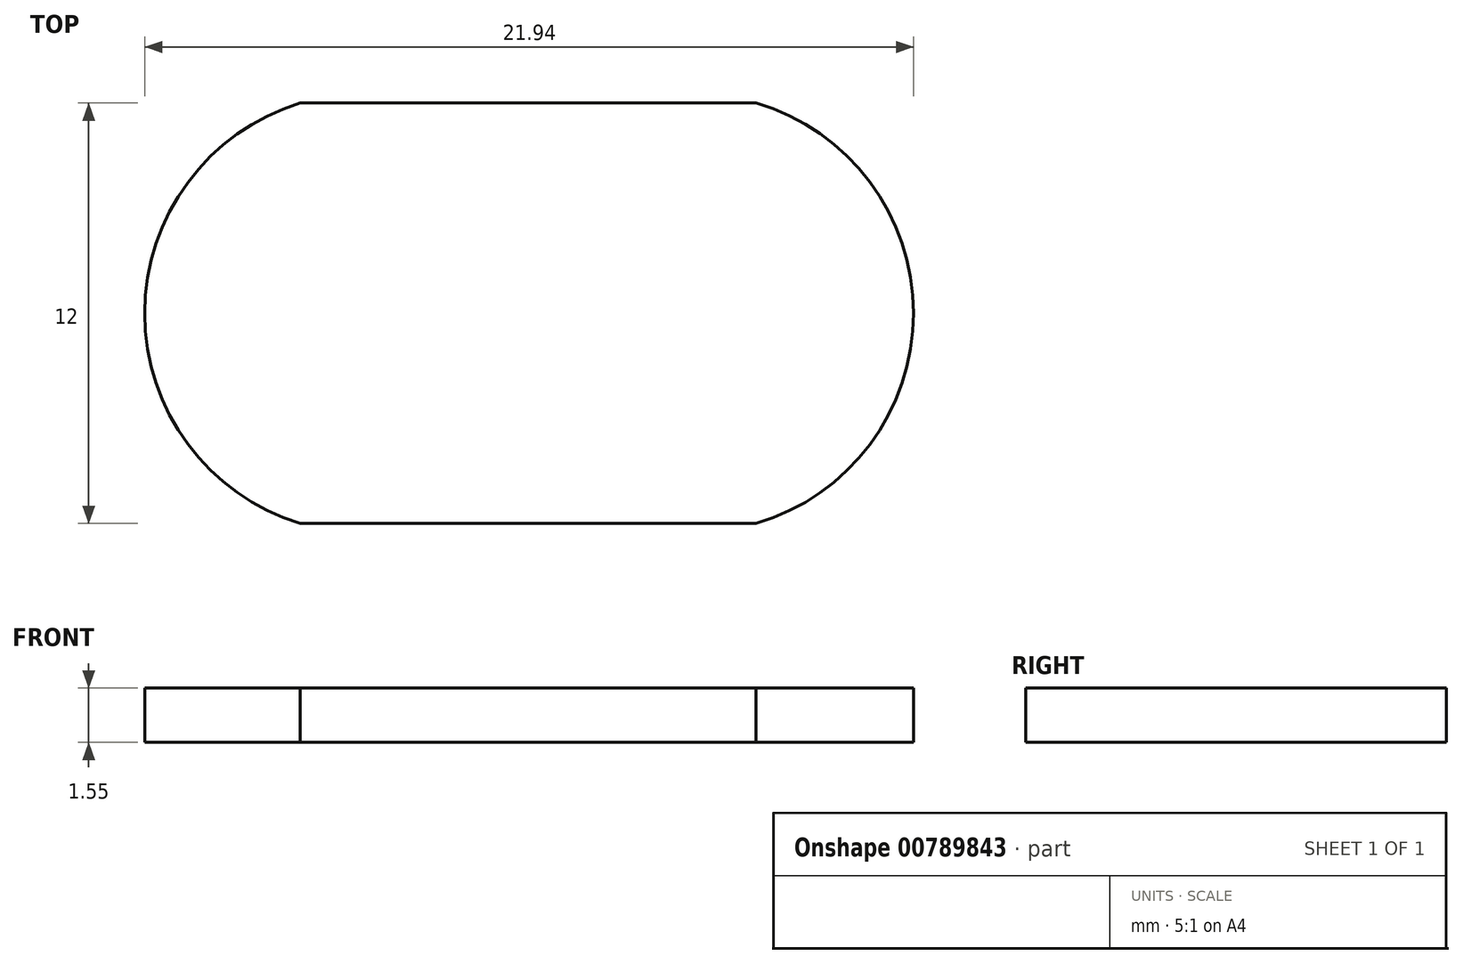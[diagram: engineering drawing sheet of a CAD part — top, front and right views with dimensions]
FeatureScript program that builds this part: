
annotation { "Feature Type Name" : "Feature", "Feature Type Description" : "" }
export const myFeature = defineFeature(function(context is Context, id is Id, definition is map)
    precondition{}
    {
        {
            var Q0;
            Q0=qCreatedBy(makeId("Top.planeOp"),FACE);
            var sketch = newSketch(context, id + "F0", { "sketchPlane" : qUnion([Q0])});
            skLineSegment(sketch, "E0.bottom", {"start": v(6.5, -6) * mm, "end": v(-6.5, -6) * mm});
            skLineSegment(sketch, "E0.top", {"start": v(6.5, 6) * mm, "end": v(-6.5, 6) * mm});
            skPoint(sketch, "E0.middle", {"position": v(0, 0) * mm});
            skLineSegment(sketch, "E1", {"start": v(-11, 7.8) * mm, "end": v(-11, -7.92) * mm, "construction": true});
            skLineSegment(sketch, "E2", {"start": v(11, 7.83) * mm, "end": v(11, -8.37) * mm, "construction": true});
            skArc(sketch, "E3", {"start": v(-6.5, 6) * mm, "mid": v(-10.94, 0) * mm, "end": v(-6.5, -6) * mm});
            skArc(sketch, "E4", {"start": v(6.5, -6) * mm, "mid": v(11, 0) * mm, "end": v(6.5, 6) * mm});
            skSolve(sketch);
        }
        {
            var Q0;
            Q0=makeQuery(id+"F0.imprint","IMPRINT",FACE,{"disambiguationData":[TD([[makeQuery(id+"F0.imprint","IMPRINT",EDGE,{"derivedFrom":sQuery(id+"F0.wireOp",EDGE,"E0.bottom")}),-1.0]])]});
            extrude(context, id + "F1", {"entities" : qUnion([Q0]), "depth" : 1 * mm, "offsetDistance" : 25 * mm});
        }
        {
            var Q0;
            Q0=makeQuery(id+"F1.opExtrude","CAP_FACE",FACE,{"disambiguationData":[OSD([sQuery(id+"F0.wireOp",EDGE,"E0.bottom"),sQuery(id+"F0.wireOp",EDGE,"E0.top"),sQuery(id+"F0.wireOp",EDGE,"E3"),sQuery(id+"F0.wireOp",EDGE,"E4"),sQuery(id+"F0.wireOp",EDGE,"hc73NTCq-gwgR-1fEX-p4L1-kKxA1QA5XJSd")])],"isStart":false});
            var sketch = newSketch(context, id + "F2", { "sketchPlane" : qUnion([Q0])});
            skArc(sketch, "E5.0", {"start": v(-6.5, 6) * mm, "mid": v(-10.94, 0) * mm, "end": v(-6.5, -6) * mm});
            skLineSegment(sketch, "E5.1", {"start": v(6.5, -6) * mm, "end": v(-6.5, -6) * mm});
            skArc(sketch, "E5.2", {"start": v(6.5, -6) * mm, "mid": v(11, 0) * mm, "end": v(6.5, 6) * mm});
            skLineSegment(sketch, "E5.3", {"start": v(6.5, 6) * mm, "end": v(-6.5, 6) * mm});
            skLineSegment(sketch, "E6.0.3", {"start": v(-6.5, -6) * mm, "end": v(6.5, -6) * mm});
            skSolve(sketch);
        }
        {
            var Q0;
            Q0=qSketchRegion(id+"F2",true);
            extrude(context, id + "F3", {"entities" : qUnion([Q0]), "operationType" : NewBodyOperationType.ADD, "depth" : 0.55 * mm, "offsetDistance" : 25 * mm});
        }
    });
